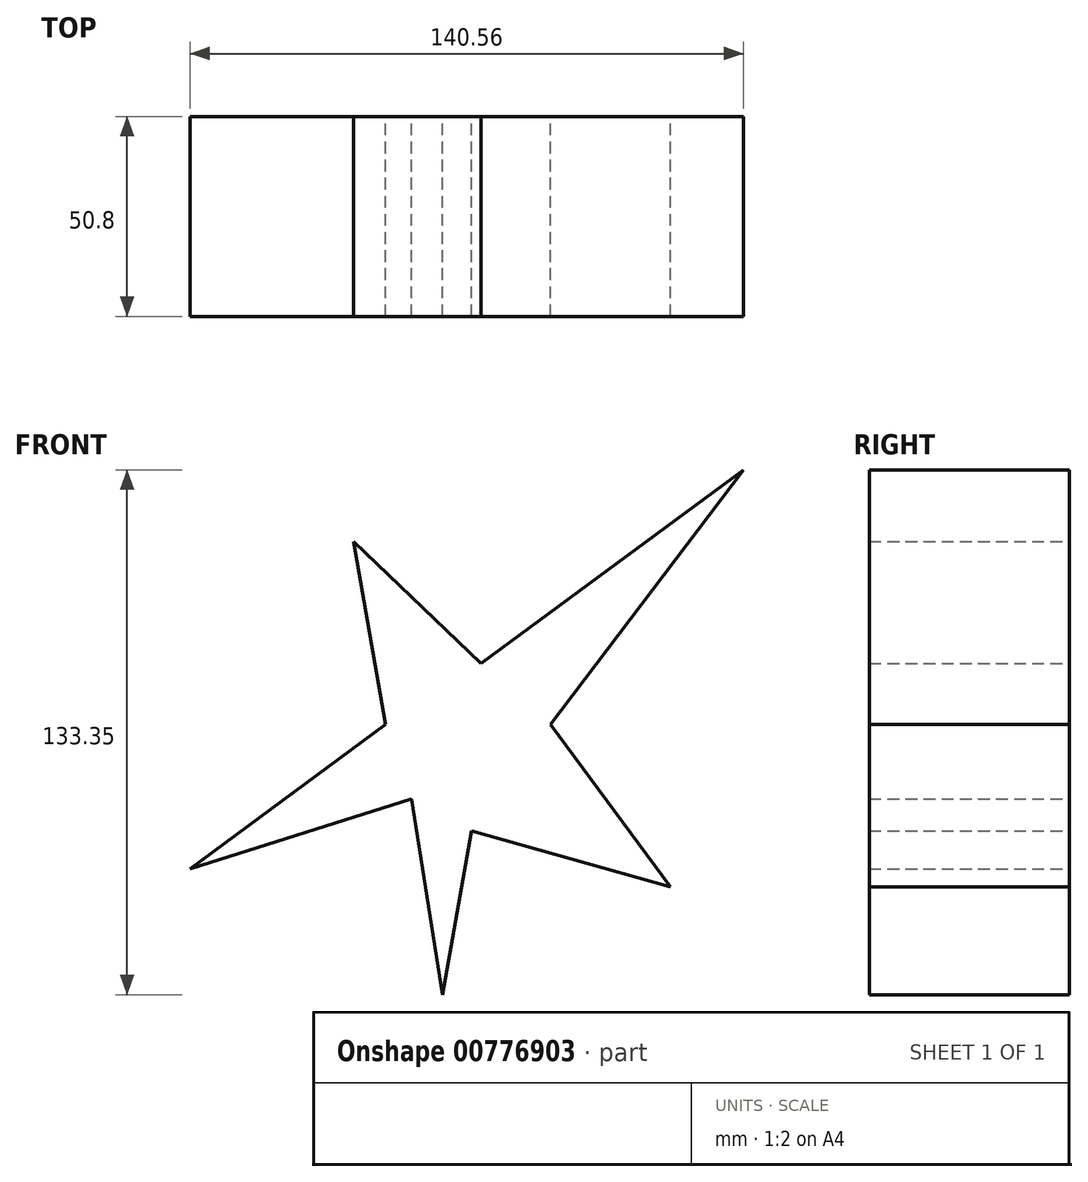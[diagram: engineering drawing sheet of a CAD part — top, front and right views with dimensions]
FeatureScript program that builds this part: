
annotation { "Feature Type Name" : "Feature", "Feature Type Description" : "" }
export const myFeature = defineFeature(function(context is Context, id is Id, definition is map)
    precondition{}
    {
        {
            var Q0;
            Q0=qCreatedBy(makeId("Front.planeOp"),FACE);
            var sketch = newSketch(context, id + "F0", { "sketchPlane" : qUnion([Q0])});
            skLineSegment(sketch, "E0", {"start": v(0, 0) * mm, "end": v(7.35, 41.57) * mm});
            skLineSegment(sketch, "E1", {"start": v(7.35, 41.57) * mm, "end": v(57.95, 27.34) * mm});
            skLineSegment(sketch, "E2", {"start": v(57.95, 27.34) * mm, "end": v(27.48, 68.6) * mm});
            skLineSegment(sketch, "E3", {"start": v(27.48, 68.6) * mm, "end": v(76.45, 133.35) * mm});
            skLineSegment(sketch, "E4", {"start": v(76.45, 133.35) * mm, "end": v(9.76, 84.1) * mm});
            skLineSegment(sketch, "E5", {"start": v(9.76, 84.1) * mm, "end": v(-22.58, 115.1) * mm});
            skLineSegment(sketch, "E6", {"start": v(-22.58, 115.1) * mm, "end": v(-14.42, 68.6) * mm});
            skLineSegment(sketch, "E7", {"start": v(-14.42, 68.6) * mm, "end": v(-64.1, 31.91) * mm});
            skLineSegment(sketch, "E8", {"start": v(-64.1, 31.91) * mm, "end": v(-7.9, 49.69) * mm});
            skLineSegment(sketch, "E9", {"start": v(-7.9, 49.69) * mm, "end": v(0, 0) * mm});
            skSolve(sketch);
        }
        {
            var Q0;
            Q0=makeQuery(id+"F0.imprint","IMPRINT",FACE,{"disambiguationData":[TD([[makeQuery(id+"F0.imprint","IMPRINT",EDGE,{"derivedFrom":sQuery(id+"F0.wireOp",EDGE,"E0")}),1.0]])]});
            extrude(context, id + "F1", {"entities" : qUnion([Q0]), "depth" : 50.8 * mm, "offsetDistance" : 25.4 * mm});
        }
    });
